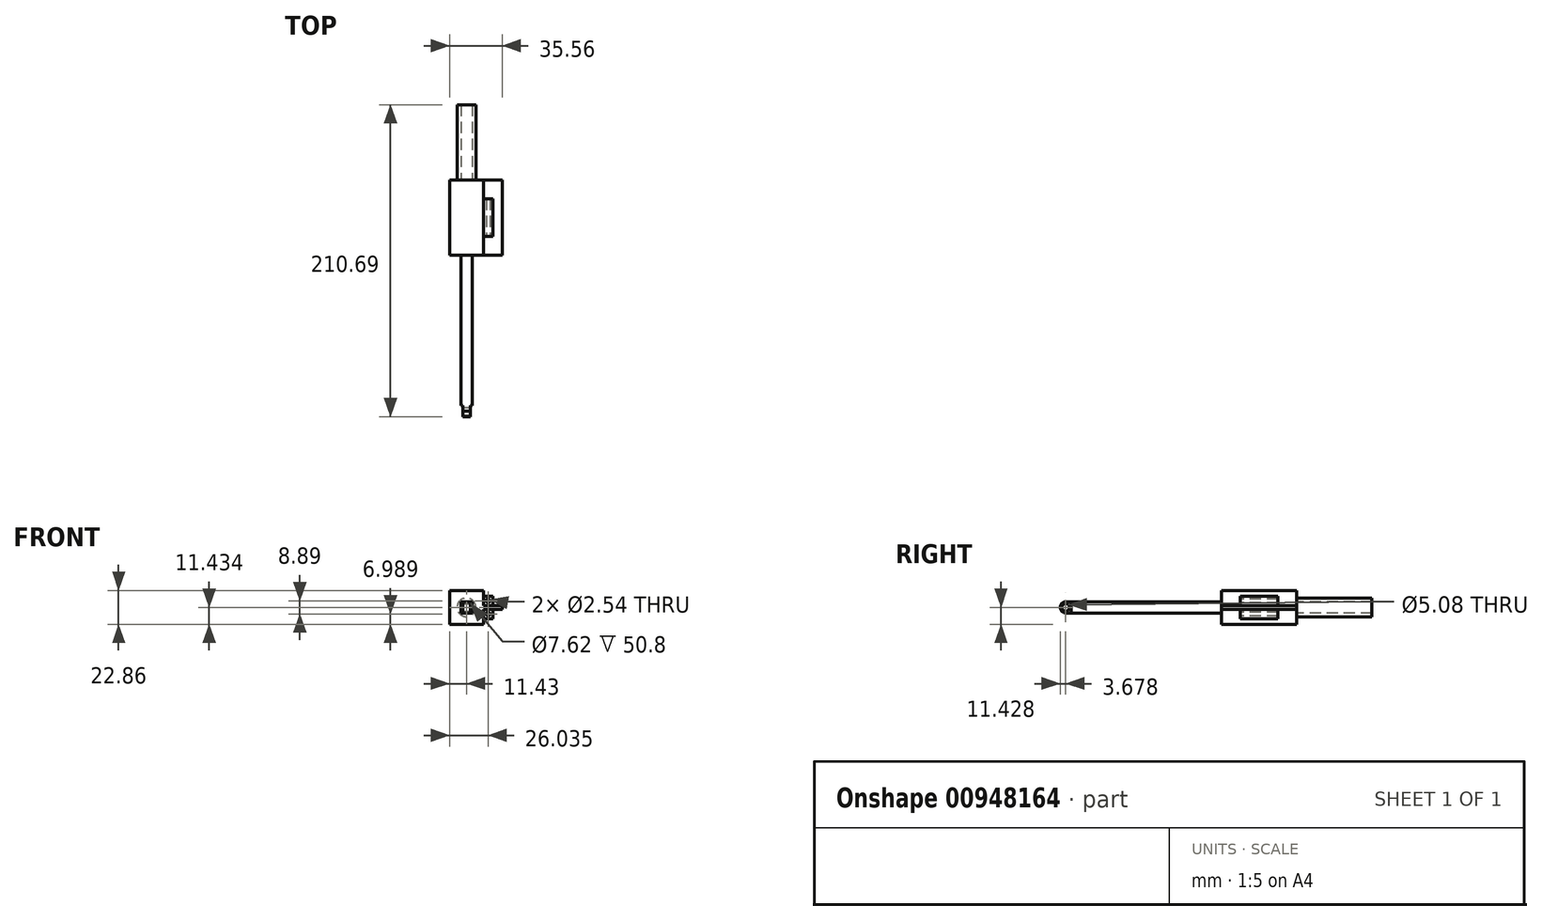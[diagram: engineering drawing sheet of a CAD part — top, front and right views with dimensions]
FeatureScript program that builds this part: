
annotation { "Feature Type Name" : "Feature", "Feature Type Description" : "" }
export const myFeature = defineFeature(function(context is Context, id is Id, definition is map)
    precondition{}
    {
        {
            var Q0;
            Q0=qCreatedBy(makeId("Right.planeOp"),FACE);
            var sketch = newSketch(context, id + "F0", { "sketchPlane" : qUnion([Q0])});
            skLineSegment(sketch, "E0.bottom", {"start": v(-52.43, 37.42) * mm, "end": v(49.17, 37.42) * mm});
            skLineSegment(sketch, "E0.top", {"start": v(-52.43, 29.8) * mm, "end": v(49.17, 29.8) * mm});
            skLineSegment(sketch, "E0.left", {"start": v(-52.43, 37.42) * mm, "end": v(-52.43, 29.8) * mm});
            skLineSegment(sketch, "E0.right", {"start": v(49.17, 37.42) * mm, "end": v(49.17, 29.8) * mm});
            skSolve(sketch);
        }
        {
            var Q0;
            Q0=makeQuery(id+"F0.imprint","IMPRINT",FACE,{"disambiguationData":[TD([[makeQuery(id+"F0.imprint","IMPRINT",EDGE,{"derivedFrom":sQuery(id+"F0.wireOp",EDGE,"E0.bottom")}),-1.0]])]});
            extrude(context, id + "F1", {"entities" : qUnion([Q0]), "depth" : 7.62 * mm, "offsetDistance" : 25.4 * mm});
        }
        {
            var Q0;
            Q0=makeQuery(id+"F1.opExtrude","SWEPT_FACE",FACE,{"disambiguationData":[OSD([sQuery(id+"F0.wireOp",EDGE,"E0.left")])]});
            var sketch = newSketch(context, id + "F2", { "sketchPlane" : qUnion([Q0])});
            skLineSegment(sketch, "E1.bottom", {"start": v(1.27, 37.42) * mm, "end": v(6.35, 37.42) * mm});
            skLineSegment(sketch, "E1.top", {"start": v(1.27, 29.8) * mm, "end": v(6.35, 29.8) * mm});
            skLineSegment(sketch, "E1.left", {"start": v(1.27, 37.42) * mm, "end": v(1.27, 29.8) * mm});
            skLineSegment(sketch, "E1.right", {"start": v(6.35, 37.42) * mm, "end": v(6.35, 29.8) * mm});
            skSolve(sketch);
        }
        {
            var Q0;
            Q0=makeQuery(id+"F2.imprint","IMPRINT",FACE,{"disambiguationData":[TD([[makeQuery(id+"F2.imprint","IMPRINT",EDGE,{"derivedFrom":sQuery(id+"F2.wireOp",EDGE,"E1.bottom")}),1.0]])]});
            extrude(context, id + "F3", {"entities" : qUnion([Q0]), "operationType" : NewBodyOperationType.ADD, "depth" : 7.62 * mm, "offsetDistance" : 25.4 * mm});
        }
        {
            var Q0;
            Q0=makeQuery(id+"F3.opExtrude","SWEPT_FACE",FACE,{"disambiguationData":[OSD([sQuery(id+"F2.wireOp",EDGE,"E1.right")])]});
            var sketch = newSketch(context, id + "F4", { "sketchPlane" : qUnion([Q0])});
            skCircle(sketch, "E2", {"center": v(-56.24, 33.6) * mm, "radius": 2.54 * mm});
            skPoint(sketch, "E2.centerSnap0", {"position": v(-60.05, 33.6) * mm});
            skArc(sketch, "E3", {"start": v(-56.24, 37.42) * mm, "mid": v(-59.92, 33.6) * mm, "end": v(-56.24, 29.8) * mm});
            skSolve(sketch);
        }
        {
            var Q0;
            Q0=makeQuery(id+"F4.imprint","IMPRINT",FACE,{"disambiguationData":[TD([[makeQuery(id+"F4.imprint","IMPRINT",EDGE,{"derivedFrom":sQuery(id+"F4.wireOp",EDGE,"E2")}),1.0]])]});
            var Q1;
            {var subQ0=sQuery(id+"F4.wireOp",EDGE,"E3");Q1=makeQuery(id+"F4.imprint","IMPRINT",FACE,{"disambiguationData":[TD([[makeQuery(id+"F4.imprint","IMPRINT",EDGE,{"derivedFrom":subQ0}),-1.0]])]});}
            extrude(context, id + "F5", {"entities" : qUnion([Q0, Q1]), "operationType" : NewBodyOperationType.REMOVE, "oppositeDirection" : true, "depth" : 25.4 * mm, "offsetDistance" : 25.4 * mm});
        }
        {
            var Q0;
            Q0=makeQuery(id+"F1.opExtrude","SWEPT_FACE",FACE,{"disambiguationData":[OSD([sQuery(id+"F0.wireOp",EDGE,"E0.right")])]});
            var sketch = newSketch(context, id + "F6", { "sketchPlane" : qUnion([Q0])});
            skLineSegment(sketch, "E4.bottom", {"start": v(7.62, 45.04) * mm, "end": v(-15.24, 45.04) * mm});
            skLineSegment(sketch, "E4.top", {"start": v(7.62, 22.18) * mm, "end": v(-15.24, 22.18) * mm});
            skLineSegment(sketch, "E4.left", {"start": v(7.62, 45.04) * mm, "end": v(7.62, 22.18) * mm});
            skLineSegment(sketch, "E4.right", {"start": v(-15.24, 45.04) * mm, "end": v(-15.24, 22.18) * mm});
            skPoint(sketch, "E4.middle", {"position": v(-3.81, 33.61) * mm});
            skPoint(sketch, "E4.middle.positionSnap0", {"position": v(-3.81, 37.42) * mm});
            skPoint(sketch, "E4.centerSnap0", {"position": v(-3.81, 37.42) * mm});
            skSolve(sketch);
        }
        {
            var Q0;
            Q0=makeQuery(id+"F6.imprint","IMPRINT",FACE,{"disambiguationData":[TD([[makeQuery(id+"F6.imprint","IMPRINT",EDGE,{"derivedFrom":sQuery(id+"F6.wireOp",EDGE,"E4.bottom")}),1.0]])]});
            var Q1;
            {var subQ0=sQuery(id+"F0.wireOp",EDGE,"E0.right");Q1=makeQuery(id+"F6.imprint","IMPRINT",FACE,{"disambiguationData":[TD([[makeQuery(id+"F6.imprint","IMPRINT",EDGE,{"derivedFrom":makeQuery(id+"F1.opExtrude","CAP_EDGE",EDGE,{"disambiguationData":[OSD([subQ0])],"isStart":true})}),-1.0]])]});}
            extrude(context, id + "F7", {"entities" : qUnion([Q0, Q1]), "operationType" : NewBodyOperationType.ADD, "depth" : 50.8 * mm, "offsetDistance" : 25.4 * mm});
        }
        {
            var Q0;
            Q0=makeQuery(id+"F7.opExtrude","CAP_FACE",FACE,{"disambiguationData":[OSD([sQuery(id+"F6.wireOp",EDGE,"E4.bottom"),sQuery(id+"F6.wireOp",EDGE,"E4.top"),sQuery(id+"F6.wireOp",EDGE,"E4.left"),sQuery(id+"F6.wireOp",EDGE,"E4.right")])],"isStart":false});
            var sketch = newSketch(context, id + "F8", { "sketchPlane" : qUnion([Q0])});
            skCircle(sketch, "E5", {"center": v(-3.81, 33.61) * mm, "radius": 3.81 * mm});
            skPoint(sketch, "E5.centerSnap0", {"position": v(-3.81, 45.04) * mm});
            skCircle(sketch, "E6", {"center": v(-3.81, 33.61) * mm, "radius": 6.35 * mm});
            skSolve(sketch);
        }
        {
            var Q0;
            Q0=makeQuery(id+"F8.imprint","IMPRINT",FACE,{"disambiguationData":[TD([[makeQuery(id+"F8.imprint","IMPRINT",EDGE,{"derivedFrom":sQuery(id+"F8.wireOp",EDGE,"E5")}),-1.0]])]});
            extrude(context, id + "F9", {"entities" : qUnion([Q0]), "operationType" : NewBodyOperationType.ADD, "depth" : 50.8 * mm, "offsetDistance" : 25.4 * mm});
        }
        {
            var Q0;
            Q0=makeQuery(id+"F7.opExtrude","SWEPT_FACE",FACE,{"disambiguationData":[OSD([sQuery(id+"F6.wireOp",EDGE,"E4.right")])]});
            var sketch = newSketch(context, id + "F10", { "sketchPlane" : qUnion([Q0])});
            skLineSegment(sketch, "E7.bottom", {"start": v(99.97, 34.88) * mm, "end": v(49.17, 34.88) * mm});
            skLineSegment(sketch, "E7.top", {"start": v(99.97, 32.34) * mm, "end": v(49.17, 32.34) * mm});
            skLineSegment(sketch, "E7.left", {"start": v(99.97, 34.88) * mm, "end": v(99.97, 32.34) * mm});
            skLineSegment(sketch, "E7.right", {"start": v(49.17, 34.88) * mm, "end": v(49.17, 32.34) * mm});
            skLineSegment(sketch, "E8", {"start": v(99.97, 34.88) * mm, "end": v(99.97, 45.04) * mm});
            skLineSegment(sketch, "E9", {"start": v(99.97, 32.34) * mm, "end": v(99.97, 22.18) * mm});
            skSolve(sketch);
        }
        {
            var Q0;
            Q0=makeQuery(id+"F10.imprint","IMPRINT",FACE,{"disambiguationData":[TD([[makeQuery(id+"F10.imprint","IMPRINT",EDGE,{"derivedFrom":sQuery(id+"F10.wireOp",EDGE,"E7.bottom")}),1.0]])]});
            extrude(context, id + "F11", {"entities" : qUnion([Q0]), "operationType" : NewBodyOperationType.ADD, "depth" : 12.7 * mm, "offsetDistance" : 25.4 * mm});
        }
        {
            var Q0;
            {var subQ0=sQuery(id+"F6.wireOp",EDGE,"E4.right");var subQ3=sQuery(id+"F6.wireOp",EDGE,"E4.bottom");Q0=makeQuery(id+"F11.boolean.opBoolean","SPLIT",FACE,{"disambiguationData":[TD([makeQuery(id+"F7.opExtrude","SWEPT_FACE",FACE,{"disambiguationData":[OSD([subQ3])]})])],"derivedFrom":makeQuery(id+"F7.opExtrude","SWEPT_FACE",FACE,{"disambiguationData":[OSD([subQ0])]})});}
            var sketch = newSketch(context, id + "F12", { "sketchPlane" : qUnion([Q0])});
            skLineSegment(sketch, "E10.bottom", {"start": v(61.87, 34.88) * mm, "end": v(87.27, 34.88) * mm});
            skLineSegment(sketch, "E10.top", {"start": v(61.87, 41.23) * mm, "end": v(87.27, 41.23) * mm});
            skLineSegment(sketch, "E10.left", {"start": v(61.87, 34.88) * mm, "end": v(61.87, 41.23) * mm});
            skLineSegment(sketch, "E10.right", {"start": v(87.27, 34.88) * mm, "end": v(87.27, 41.23) * mm});
            skLineSegment(sketch, "E11.bottom", {"start": v(64.4, 41.23) * mm, "end": v(66.95, 41.23) * mm});
            skLineSegment(sketch, "E11.top", {"start": v(64.4, 34.88) * mm, "end": v(66.95, 34.88) * mm});
            skLineSegment(sketch, "E11.left", {"start": v(64.4, 41.23) * mm, "end": v(64.4, 34.88) * mm});
            skLineSegment(sketch, "E11.right", {"start": v(66.95, 41.23) * mm, "end": v(66.95, 34.88) * mm});
            skLineSegment(sketch, "E12.bottom", {"start": v(82.19, 41.23) * mm, "end": v(84.73, 41.23) * mm});
            skLineSegment(sketch, "E12.top", {"start": v(82.19, 34.88) * mm, "end": v(84.73, 34.88) * mm});
            skLineSegment(sketch, "E12.left", {"start": v(82.19, 41.23) * mm, "end": v(82.19, 34.88) * mm});
            skLineSegment(sketch, "E12.right", {"start": v(84.73, 41.23) * mm, "end": v(84.73, 34.88) * mm});
            skSolve(sketch);
        }
        {
            var Q0;
            Q0=makeQuery(id+"F12.imprint","IMPRINT",FACE,{"disambiguationData":[TD([[makeQuery(id+"F12.imprint","IMPRINT",EDGE,{"derivedFrom":sQuery(id+"F12.wireOp",EDGE,"E10.bottom")}),-1.0]])]});
            extrude(context, id + "F13", {"entities" : qUnion([Q0]), "operationType" : NewBodyOperationType.ADD, "depth" : 6.35 * mm, "offsetDistance" : 25.4 * mm});
        }
        {
            var Q0;
            {var subQ0=sQuery(id+"F6.wireOp",EDGE,"E4.top");var subQ1=sQuery(id+"F6.wireOp",EDGE,"E4.right");Q0=makeQuery(id+"F11.boolean.opBoolean","SPLIT",FACE,{"disambiguationData":[TD([makeQuery(id+"F7.opExtrude","SWEPT_FACE",FACE,{"disambiguationData":[OSD([subQ0])]})])],"derivedFrom":makeQuery(id+"F7.opExtrude","SWEPT_FACE",FACE,{"disambiguationData":[OSD([subQ1])]})});}
            var sketch = newSketch(context, id + "F14", { "sketchPlane" : qUnion([Q0])});
            skLineSegment(sketch, "E13.bottom", {"start": v(61.87, 32.34) * mm, "end": v(87.27, 32.34) * mm});
            skLineSegment(sketch, "E13.top", {"start": v(61.87, 26) * mm, "end": v(87.27, 26) * mm});
            skLineSegment(sketch, "E13.left", {"start": v(61.87, 32.34) * mm, "end": v(61.87, 26) * mm});
            skLineSegment(sketch, "E13.right", {"start": v(87.27, 32.34) * mm, "end": v(87.27, 26) * mm});
            skLineSegment(sketch, "E14.bottom", {"start": v(64.4, 32.34) * mm, "end": v(66.95, 32.34) * mm});
            skLineSegment(sketch, "E14.top", {"start": v(64.4, 26) * mm, "end": v(66.95, 26) * mm});
            skLineSegment(sketch, "E14.left", {"start": v(64.4, 32.34) * mm, "end": v(64.4, 26) * mm});
            skLineSegment(sketch, "E14.right", {"start": v(66.95, 32.34) * mm, "end": v(66.95, 26) * mm});
            skLineSegment(sketch, "E15.bottom", {"start": v(82.19, 32.34) * mm, "end": v(84.73, 32.34) * mm});
            skLineSegment(sketch, "E15.top", {"start": v(82.19, 26) * mm, "end": v(84.73, 26) * mm});
            skLineSegment(sketch, "E15.left", {"start": v(82.19, 32.34) * mm, "end": v(82.19, 26) * mm});
            skLineSegment(sketch, "E15.right", {"start": v(84.73, 32.34) * mm, "end": v(84.73, 26) * mm});
            skSolve(sketch);
        }
        {
            var Q0;
            Q0=makeQuery(id+"F14.imprint","IMPRINT",FACE,{"disambiguationData":[TD([[makeQuery(id+"F14.imprint","IMPRINT",EDGE,{"derivedFrom":sQuery(id+"F14.wireOp",EDGE,"E13.bottom")}),1.0]])]});
            extrude(context, id + "F15", {"entities" : qUnion([Q0]), "operationType" : NewBodyOperationType.ADD, "depth" : 6.35 * mm, "offsetDistance" : 25.4 * mm});
        }
        {
            var Q0;
            Q0=makeQuery(id+"F13.opExtrude","SWEPT_FACE",FACE,{"disambiguationData":[OSD([sQuery(id+"F12.wireOp",EDGE,"E10.left")])]});
            var sketch = newSketch(context, id + "F16", { "sketchPlane" : qUnion([Q0])});
            skCircle(sketch, "E16", {"center": v(18.41, 38.06) * mm, "radius": 1.27 * mm});
            skPoint(sketch, "E16.centerSnap0", {"position": v(18.42, 41.23) * mm});
            skSolve(sketch);
        }
        {
            var Q0;
            Q0=makeQuery(id+"F16.imprint","IMPRINT",FACE,{"disambiguationData":[TD([[makeQuery(id+"F16.imprint","IMPRINT",EDGE,{"derivedFrom":sQuery(id+"F16.wireOp",EDGE,"E16")}),1.0]])]});
            extrude(context, id + "F17", {"entities" : qUnion([Q0]), "operationType" : NewBodyOperationType.REMOVE, "oppositeDirection" : true, "depth" : 25.4 * mm, "offsetDistance" : 25.4 * mm});
        }
        {
            var Q0;
            Q0=makeQuery(id+"F15.opExtrude","SWEPT_FACE",FACE,{"disambiguationData":[OSD([sQuery(id+"F14.wireOp",EDGE,"E13.left")])]});
            var sketch = newSketch(context, id + "F18", { "sketchPlane" : qUnion([Q0])});
            skCircle(sketch, "E17", {"center": v(18.41, 29.17) * mm, "radius": 1.27 * mm});
            skPoint(sketch, "E17.centerSnap0", {"position": v(18.41, 26) * mm});
            skSolve(sketch);
        }
        {
            var Q0;
            Q0=makeQuery(id+"F18.imprint","IMPRINT",FACE,{"disambiguationData":[TD([[makeQuery(id+"F18.imprint","IMPRINT",EDGE,{"derivedFrom":sQuery(id+"F18.wireOp",EDGE,"E17")}),1.0]])]});
            extrude(context, id + "F19", {"entities" : qUnion([Q0]), "operationType" : NewBodyOperationType.REMOVE, "oppositeDirection" : true, "depth" : 25.4 * mm, "offsetDistance" : 25.4 * mm});
        }
    });
